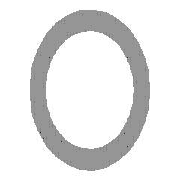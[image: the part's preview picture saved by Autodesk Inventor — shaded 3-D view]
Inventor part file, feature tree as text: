
AUTODESK INVENTOR PART (.ipt)
format: ipt  version: 2013 (Build 170138000, 138)  size: 114,688 bytes
history: native  units: mm (DEFAULTED — no unit token found)
features: other x4, sketch x3, plane x1
ambient origin geometry x8: Origin, YZ Plane, XZ Plane, XY Plane, X Axis, Y Axis, Z Axis, Center Point
bodies: Solid1 (feature_tree), Body (feature_tree)
feature tree (8):
  parser-record x1  (decoder bookkeeping rows leaked as tree rows — omitted from the tree; the rows remain in map.json)
  other  "Driven Length"
  other  "Start plane"
  other  "End plane"
  sketch  "Sketch"  dims[d2=63.5mm d3=0.0mm d4=-0.0mm d5=63.5mm d6=90.0deg d7=63.5mm]
  sketch  "Sketch3"  dims[d0=42.164mm]
  plane  "Work Plane3"
  sketch  "Sketch4"  dims[d1=3.556mm]
